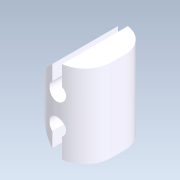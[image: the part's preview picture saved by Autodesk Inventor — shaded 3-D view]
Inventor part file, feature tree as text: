
AUTODESK INVENTOR PART (.ipt)
format: ipt  version: 2020.2 (Build 242310000, 310)  size: 162,304 bytes
history: native  units: mm
features: extrude x3, sketch x3, fillet x1
ambient origin geometry x8: Origin, YZ Plane, XZ Plane, XY Plane, X Axis, Y Axis, Z Axis, Center Point
bodies: Solid1 (feature_tree)
feature tree (7):
  extrude  "Extrusion1"  Depth=25.0mm
  extrude  "Extrusion2"  Depth=17.0mm
  fillet  "Fillet1"  Radius=17.0mm
  extrude  "Extrusion4"  TaperAngle=0.0deg  [1 undecoded]
  sketch  "Sketch1"  dims[d1=2.5mm d2=25.0mm]
  sketch  "Sketch2"  dims[d3=5.0mm d5=17.0mm d9=17.0mm]
  sketch  "Sketch4"  dims[d10=2.5mm d11=0.0mm d12=135.0deg d13=135.0deg d14=20.0mm d15=0.0mm d16=8.0mm d17=5.0mm d18=1.5mm d19=3.0mm d20=8.0mm d21=1.5mm d22=1.5mm d23=5.0mm d24=0.0mm d25=0.0mm d26=8.0mm d31=2.0mm d32=2.0mm d33=0.0mm d34=0.0mm]
note: 1 required parameter value undecoded (feature->parameter linkage not recoverable at this tier; creation-order binding heuristic only, values carry confidence <= 0.55)
